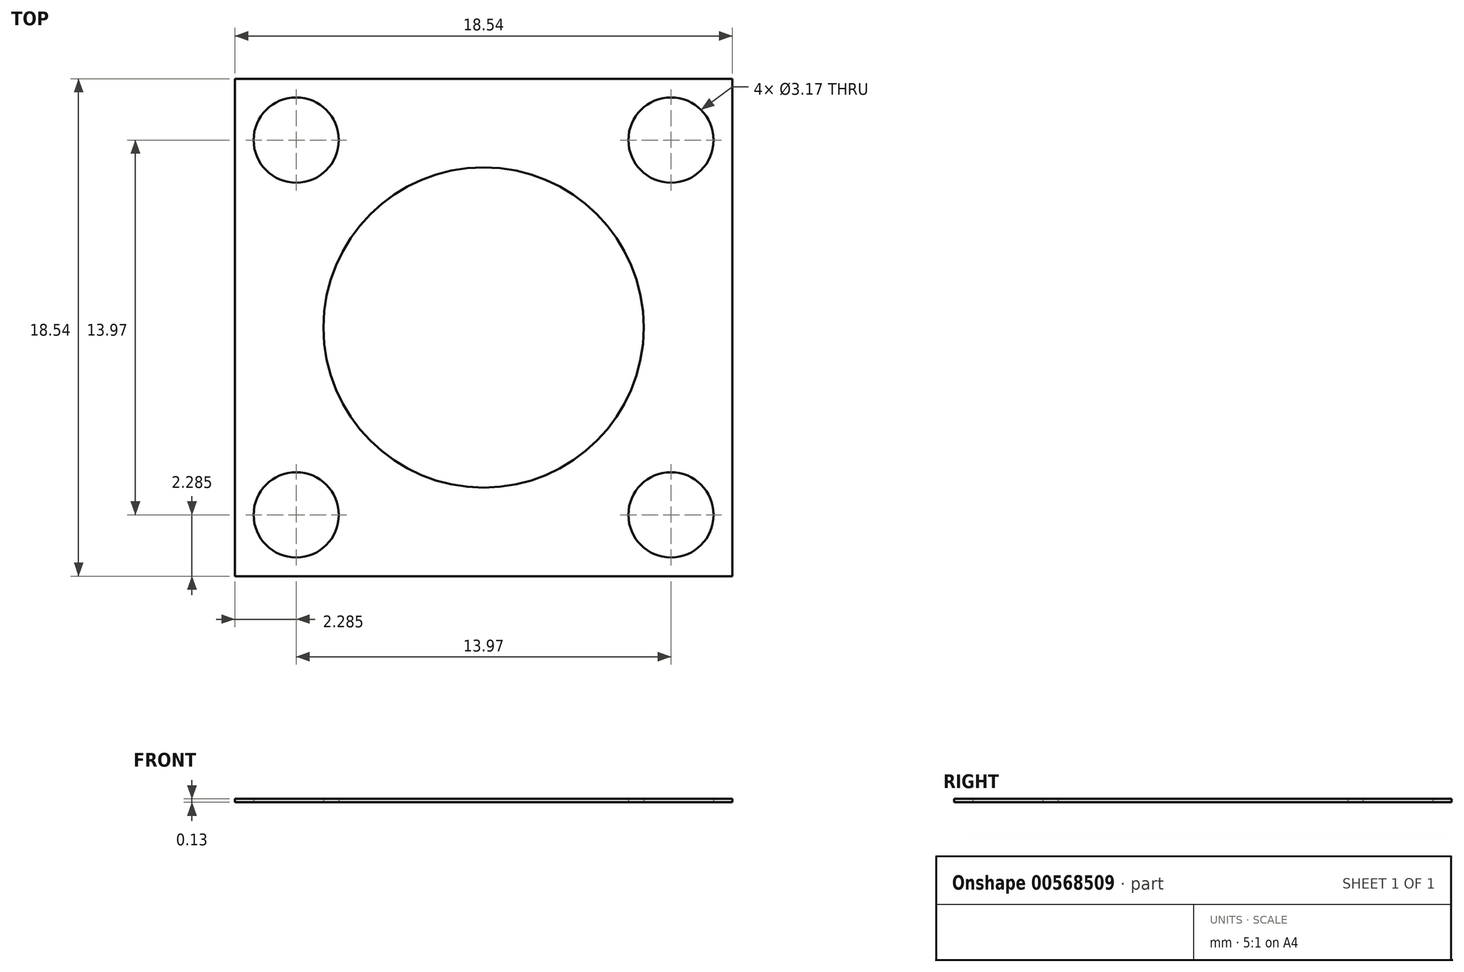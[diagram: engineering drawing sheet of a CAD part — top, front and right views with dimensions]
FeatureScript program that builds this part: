
annotation { "Feature Type Name" : "Feature", "Feature Type Description" : "" }
export const myFeature = defineFeature(function(context is Context, id is Id, definition is map)
    precondition{}
    {
        {
            var Q0;
            Q0=qCreatedBy(makeId("Top.planeOp"),FACE);
            var sketch = newSketch(context, id + "F0", { "sketchPlane" : qUnion([Q0])});
            skLineSegment(sketch, "E0.bottom", {"start": v(-9.27, 9.27) * mm, "end": v(9.27, 9.27) * mm});
            skLineSegment(sketch, "E0.top", {"start": v(-9.27, -9.27) * mm, "end": v(9.27, -9.27) * mm});
            skLineSegment(sketch, "E0.left", {"start": v(-9.27, 9.27) * mm, "end": v(-9.27, -9.27) * mm});
            skLineSegment(sketch, "E0.right", {"start": v(9.27, 9.27) * mm, "end": v(9.27, -9.27) * mm});
            skPoint(sketch, "E0.middle", {"position": v(0, 0) * mm});
            skCircle(sketch, "E1", {"center": v(-6.99, 6.99) * mm, "radius": 1.59 * mm});
            skCircle(sketch, "E2", {"center": v(0, 0) * mm, "radius": 5.97 * mm});
            skCircle(sketch, "E3.0.1.0", {"center": v(-6.99, -6.99) * mm, "radius": 1.59 * mm});
            skCircle(sketch, "E3.1.0.0", {"center": v(6.99, 6.99) * mm, "radius": 1.59 * mm});
            skCircle(sketch, "E3.1.1.0", {"center": v(6.99, -6.99) * mm, "radius": 1.59 * mm});
            skLineSegment(sketch, "E3.direction1", {"start": v(-6.99, 6.99) * mm, "end": v(6.99, 6.99) * mm, "construction": true});
            skLineSegment(sketch, "E3.direction2", {"start": v(-6.99, 6.99) * mm, "end": v(-6.99, -6.99) * mm, "construction": true});
            skSolve(sketch);
        }
        {
            var Q0;
            Q0 = qSketchRegion(id + "F0", true);
            extrude(context, id + "F1", {"entities" : qUnion([Q0]), "depth" : 0.13 * mm, "offsetDistance" : 25.4 * mm});
        }
    });
